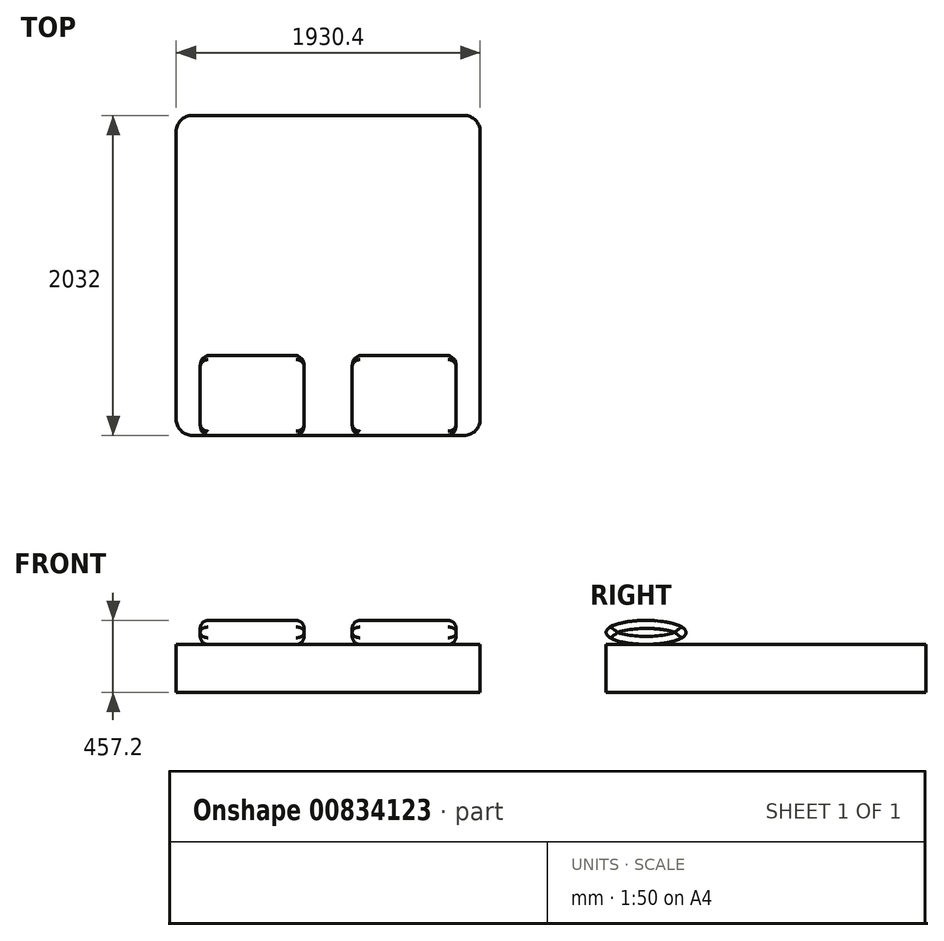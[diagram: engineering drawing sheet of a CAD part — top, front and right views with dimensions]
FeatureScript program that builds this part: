
annotation { "Feature Type Name" : "Feature", "Feature Type Description" : "" }
export const myFeature = defineFeature(function(context is Context, id is Id, definition is map)
    precondition{}
    {
        {
            var Q0;
            Q0=qCreatedBy(makeId("Top.planeOp"),FACE);
            var sketch = newSketch(context, id + "F0", { "sketchPlane" : qUnion([Q0])});
            skLineSegment(sketch, "E0.rect.bottom", {"start": v(-965.2, -1016) * mm, "end": v(965.2, -1016) * mm});
            skLineSegment(sketch, "E0.rect.top", {"start": v(-965.2, 1016) * mm, "end": v(965.2, 1016) * mm});
            skLineSegment(sketch, "E0.rect.left", {"start": v(-965.2, -1016) * mm, "end": v(-965.2, 1016) * mm});
            skLineSegment(sketch, "E0.rect.right", {"start": v(965.2, -1016) * mm, "end": v(965.2, 1016) * mm});
            skPoint(sketch, "E0.rect.middle", {"position": v(0, 0) * mm});
            skSolve(sketch);
        }
        {
            var Q0;
            Q0=qSketchRegion(id+"F0",true);
            extrude(context, id + "F1", {"entities" : qUnion([Q0]), "depth" : 304.8 * mm});
        }
        {
            var Q0;
            Q0=makeQuery(id+"F1.opExtrude","SWEPT_EDGE",EDGE,{"disambiguationData":[OSD([sQuery(id+"F0.wireOp",EDGE,"E0.rect.top"),sQuery(id+"F0.wireOp",EDGE,"E0.rect.left")])]});
            var Q1;
            Q1=makeQuery(id+"F1.opExtrude","SWEPT_EDGE",EDGE,{"disambiguationData":[OSD([sQuery(id+"F0.wireOp",EDGE,"E0.rect.top"),sQuery(id+"F0.wireOp",EDGE,"E0.rect.right")])]});
            var Q2;
            Q2=makeQuery(id+"F1.opExtrude","SWEPT_EDGE",EDGE,{"disambiguationData":[OSD([sQuery(id+"F0.wireOp",EDGE,"E0.rect.bottom"),sQuery(id+"F0.wireOp",EDGE,"E0.rect.left")])]});
            var Q3;
            Q3=makeQuery(id+"F1.opExtrude","SWEPT_EDGE",EDGE,{"disambiguationData":[OSD([sQuery(id+"F0.wireOp",EDGE,"E0.rect.bottom"),sQuery(id+"F0.wireOp",EDGE,"E0.rect.right")])]});
            fillet(context, id + "F2", {"entities" : qUnion([Q0, Q1, Q2, Q3]), "radius" : 101.6 * mm, "tangentPropagation" : true, "allowEdgeOverflow" : false});
        }
        {
            var Q0;
            Q0=qCreatedBy(makeId("Right.planeOp"),FACE);
            cPlane(context, id + "F3", {"entities" : qUnion([Q0]), "cplaneType" : CPlaneType.OFFSET, "offset" : 482.6 * mm, "width" : 152.4 * mm, "height" : 152.4 * mm});
        }
        {
            var Q0;
            Q0=qCreatedBy(id+"F3.planeOp",FACE);
            var sketch = newSketch(context, id + "F4", { "sketchPlane" : qUnion([Q0])});
            skEllipse(sketch, "E1", {"center": v(-762, 381) * mm, "majorRadius": 254 * mm, "minorRadius": 76.2 * mm, "majorAxis": v(1, 0)});
            skLineSegment(sketch, "E2", {"start": v(-762, 457.2) * mm, "end": v(-762, 304.8) * mm, "construction": true});
            skSolve(sketch);
        }
        {
            var Q0;
            Q0=qSketchRegion(id+"F4",true);
            extrude(context, id + "F5", {"entities" : qUnion([Q0]), "operationType" : NewBodyOperationType.ADD, "endBound" : BoundingType.SYMMETRIC, "depth" : 660.4 * mm});
        }
        {
            var Q0;
            Q0=makeQuery(id+"F5.opExtrude","SWEPT_BODY",BODY,{"disambiguationData":[OSD([sQuery(id+"F4.wireOp",EDGE,"E1")])]});
            var Q1;
            Q1=qCreatedBy(makeId("Right.planeOp"),FACE);
            mirror(context, id + "F6", {"operationType" : NewBodyOperationType.ADD, "entities" : qUnion([Q0]), "mirrorPlane" : qUnion([Q1])});
        }
        {
            var Q0;
            Q0=makeQuery(id+"F6.opPattern","COPY",EDGE,{"derivedFrom":makeQuery(id+"F5.opExtrude","CAP_EDGE",EDGE,{"disambiguationData":[OSD([sQuery(id+"F4.wireOp",EDGE,"E1")])],"isStart":true}),"instanceName":"1"});
            fillet(context, id + "F7", {"entities" : qUnion([Q0]), "radius" : 50.8 * mm, "tangentPropagation" : true, "allowEdgeOverflow" : false});
        }
        {
            var Q0;
            Q0=makeQuery(id+"F6.opPattern","COPY",EDGE,{"derivedFrom":makeQuery(id+"F5.opExtrude","CAP_EDGE",EDGE,{"disambiguationData":[OSD([sQuery(id+"F4.wireOp",EDGE,"E1")])],"isStart":false}),"instanceName":"1"});
            var Q1;
            Q1=makeQuery(id+"F5.opExtrude","CAP_EDGE",EDGE,{"disambiguationData":[OSD([sQuery(id+"F4.wireOp",EDGE,"E1")])],"isStart":true});
            var Q2;
            Q2=makeQuery(id+"F5.opExtrude","CAP_EDGE",EDGE,{"disambiguationData":[OSD([sQuery(id+"F4.wireOp",EDGE,"E1")])],"isStart":false});
            fillet(context, id + "F8", {"entities" : qUnion([Q0, Q1, Q2]), "radius" : 50.8 * mm, "tangentPropagation" : true, "allowEdgeOverflow" : false});
        }
    });
